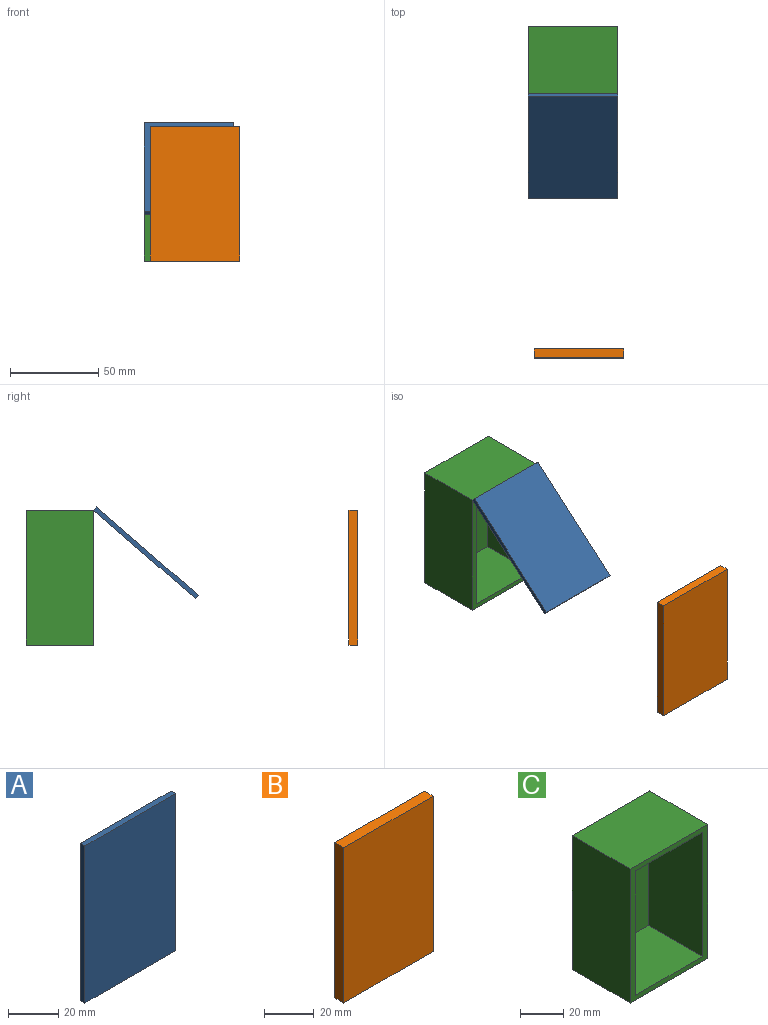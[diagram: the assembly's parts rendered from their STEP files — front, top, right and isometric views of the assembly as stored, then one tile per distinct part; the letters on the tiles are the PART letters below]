
ASSEMBLY  parts=3 mates=2
PART A: 6 faces, bbox 50.8x2.5x76.2 mm
  f0: plane 50.8x2.54mm, normal (0,0,-1), area 129mm2, adj f1,f3,f4,f5
  f1: plane 76.2x2.54mm, normal (1,0,0), area 193.5mm2, adj f0,f2,f4,f5
  f2: plane 50.8x2.54mm, normal (0,0,1), area 129mm2, adj f1,f3,f4,f5
  f3: plane 76.2x2.54mm, normal (-1,0,0), area 193.5mm2, adj f0,f2,f4,f5
  f4: plane 76.2x50.8mm, normal (0,-1,0), area 3871mm2, adj f0,f1,f2,f3
  f5: plane 76.2x50.8mm, normal (0,1,0), area 3871mm2, adj f0,f1,f2,f3
PART B: 6 faces, bbox 50.8x5.1x76.2 mm
  f0: plane 50.8x5.08mm, normal (0,0,-1), area 258.1mm2, adj f1,f3,f4,f5
  f1: plane 76.2x5.08mm, normal (1,0,0), area 387.1mm2, adj f0,f2,f4,f5
  f2: plane 50.8x5.08mm, normal (0,0,1), area 258.1mm2, adj f1,f3,f4,f5
  f3: plane 76.2x5.08mm, normal (-1,0,0), area 387.1mm2, adj f0,f2,f4,f5
  f4: plane 76.2x50.8mm, normal (0,-1,0), area 3871mm2, adj f0,f1,f2,f3
  f5: plane 76.2x50.8mm, normal (0,1,0), area 3871mm2, adj f0,f1,f2,f3
PART C: 11 faces, bbox 50.8x38.1x76.2 mm
  f0: plane 76.2x38.1mm, normal (-1,0,0), area 2903.2mm2, adj f1,f7,f8,f9
  f1: plane 50.8x38.1mm, normal (0,0,-1), area 1935.5mm2, adj f0,f2,f8,f9
  f2: plane 76.2x38.1mm, normal (1,0,0), area 2903.2mm2, adj f1,f7,f8,f9
  f3: plane 44.03x35.56mm, normal (0,0,1), area 1565.6mm2, adj f4,f6,f8,f10
  f4: plane 70.71x35.56mm, normal (1,0,0), area 2514.5mm2, adj f3,f5,f8,f10
  f5: plane 44.03x35.56mm, normal (0,0,-1), area 1565.6mm2, adj f4,f6,f8,f10
  f6: plane 70.71x35.56mm, normal (-1,0,0), area 2514.5mm2, adj f3,f5,f8,f10
  f7: plane 50.8x38.1mm, normal (0,0,1), area 1935.5mm2, adj f0,f2,f8,f9
  f8: plane 76.2x50.8mm, normal (0,-1,0), area 757.7mm2, adj f0,f1,f2,f3,f4,f5,f6,f7
  f9: plane 76.2x50.8mm, normal (0,1,0), area 3871mm2, adj f0,f1,f2,f7
  f10: plane 70.71x44.03mm, normal (0,-1,0), area 3113.3mm2, adj f3,f4,f5,f6
PLACE A rot(axis=(-1,0,0),49.1deg) t=(0.65,-65.35,83.68)mm
PLACE B t=(4.04,-184.04,67.95)mm
PLACE C t=(0.65,-1.39,67.95)mm fixed
MATE slider B.f4 <-> C.f10  axis (0,-1,0) through (-21.36,-189.12,67.95)mm
MATE revolute A.f1 <-> C.f2  axis (-1,0,0) through (26.05,-39.49,106.05)mm
